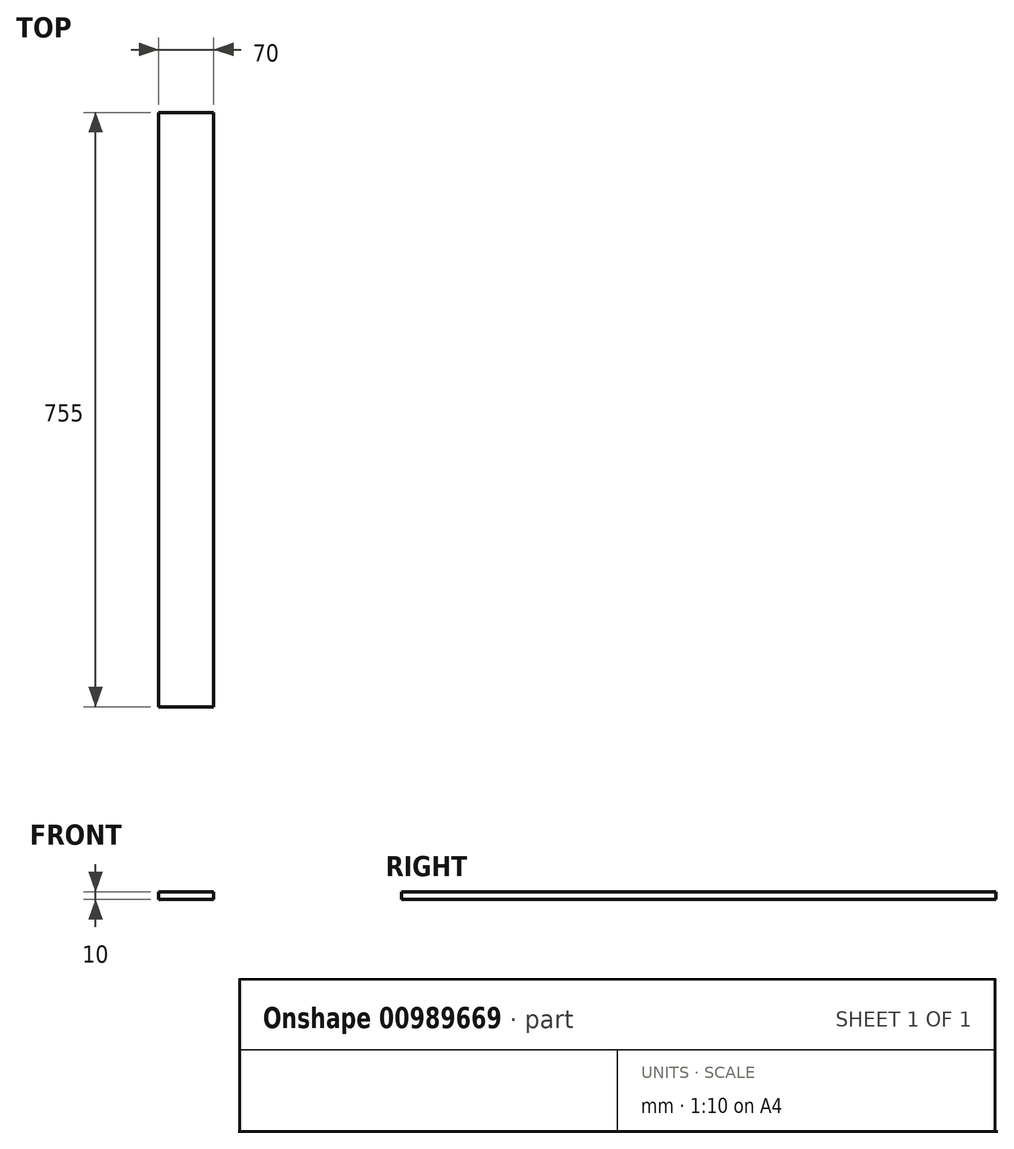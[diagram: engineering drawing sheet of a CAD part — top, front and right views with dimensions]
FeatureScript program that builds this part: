
annotation { "Feature Type Name" : "Feature", "Feature Type Description" : "" }
export const myFeature = defineFeature(function(context is Context, id is Id, definition is map)
    precondition{}
    {
        {
            var Q0;
            Q0=qCreatedBy(makeId("Front.planeOp"),FACE);
            var sketch = newSketch(context, id + "F0", { "sketchPlane" : qUnion([Q0])});
            skLineSegment(sketch, "E0.bottom", {"start": v(0, 0) * mm, "end": v(70, 0) * mm});
            skLineSegment(sketch, "E0.top", {"start": v(0, 10) * mm, "end": v(70, 10) * mm});
            skLineSegment(sketch, "E0.left", {"start": v(0, 0) * mm, "end": v(0, 10) * mm});
            skLineSegment(sketch, "E0.right", {"start": v(70, 0) * mm, "end": v(70, 10) * mm});
            skSolve(sketch);
        }
        {
            var Q0;
            Q0 = qSketchRegion(id + "F0", true);
            extrude(context, id + "F1", {"entities" : qUnion([Q0]), "depth" : 755 * mm, "offsetDistance" : 25 * mm});
        }
    });
